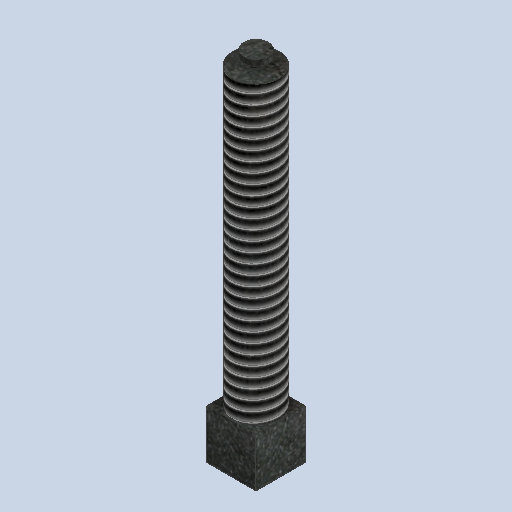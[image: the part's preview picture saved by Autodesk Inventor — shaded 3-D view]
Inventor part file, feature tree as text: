
AUTODESK INVENTOR PART (.ipt)
format: ipt  version: 2023.2 (Build 272271000, 271)  size: 293,376 bytes
history: native  units: mm
features: extrude x4, sketch x4, thread x1
ambient origin geometry x8: Origin, YZ Plane, XZ Plane, XY Plane, X Axis, Y Axis, Z Axis, Center Point
bodies: Solid1 (feature_tree)
feature tree (9):
  extrude  "Extrusion1"  Depth=20.0mm
  extrude  "Extrusion2"  Depth=20.0mm
  extrude  "Extrusion3"  Depth=120.0mm
  extrude  "Extrusion4"  Depth=10.0mm
  thread  "Thread1"  [1 undecoded]
  sketch  "Sketch1"  dims[d0=20.0mm d1=20.0mm]
  sketch  "Sketch2"  dims[d2=20.0mm d3=0.0mm d4=19.0mm]
  sketch  "Sketch3"  dims[d5=120.0mm d6=0.0mm d7=4.0mm]
  sketch  "Sketch4"  dims[d8=3.0mm d9=0.0mm d10=10.0mm d11=2.5mm d12=0.0mm d13=120.0mm d14=0.0mm]
note: 1 required parameter value undecoded (feature->parameter linkage not recoverable at this tier; creation-order binding heuristic only, values carry confidence <= 0.55)
